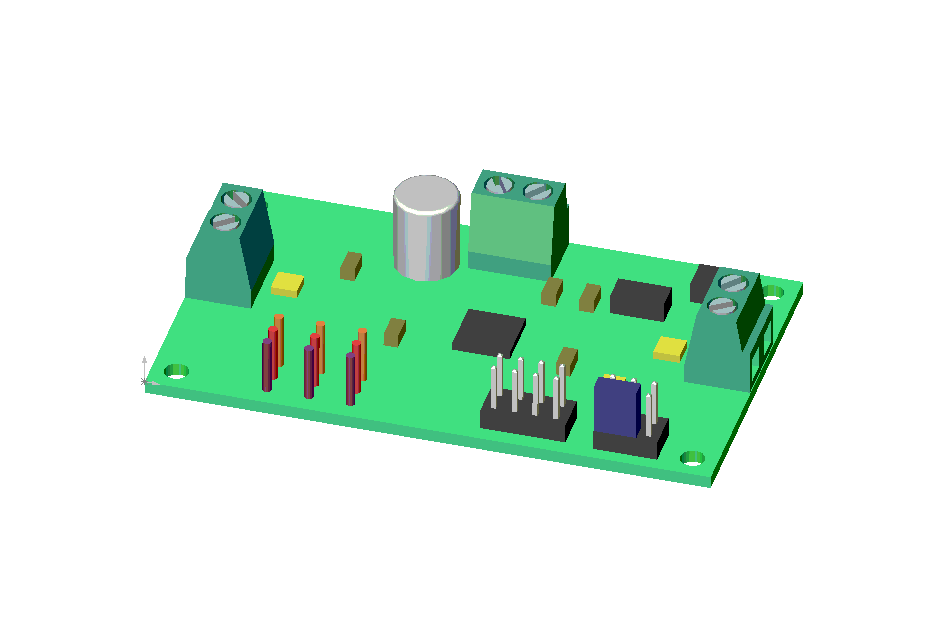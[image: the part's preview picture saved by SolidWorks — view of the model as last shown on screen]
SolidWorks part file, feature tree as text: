
SOLIDWORKS PART (.sldprt)
format: sldprt  version: not decoded by parser v0  size: 1,186,816 bytes
history: native  units: mm
features: sketch x24, extrude x15, cut_extrude x9, fillet x1, chamfer x1 (+8 scaffold rows collapsed)
feature tree (58):
  scaffold x8  (default folders/planes/origin — collapsed)
  sketch  "Sketch1"  dims[c1.D3=3.048mm c1.D4=3.05mm c1.D5=3.05mm c1.D6=3.05mm c2.D3=3.05mm c2.D1=69.0mm c2.D2=40.15mm c2.D7=3.05mm c2.D8=3.05mm c2.D9=3.05mm c2.D10=3.05mm]
  extrude  "Base-Extrude"  Depth=1.5748mm
  sketch  "Sketch2"  dims[c1.D1=12.7mm c1.D2=10.1mm c1.D3=10.1mm c1.D4=10.1mm c1.D5=8.1mm c1.D6=8.1mm c1.D7=8.1mm c1.D8=12.7mm c1.D9=28.5mm c2.D5=0.1mm c2.D6=0.1mm c2.D10=0.1mm c2.D11=8.0mm c2.D7=8.0mm c2.D12=8.0mm]
  extrude  "Boss-Extrude1"  Depth=9.94mm
  sketch  "Sketch3"  dims[c1.D1=4.3mm c1.D2=0.96mm c1.D3=1.7mm c1.D4=7.5mm c1.D5=1.45mm c1.D6=1.45mm c1.D7=7.5mm c1.D8=0.96mm c1.D9=0.96mm c2.D9=90.0deg c3.D9=1.7mm c3.D10=4.3mm]
  cut_extrude  "Cut-Extrude1"  [1 undecoded]
  sketch  "Sketch4"  dims[D1=0.96mm D2=4.3mm D3=1.7mm D4=1.45mm D5=7.5mm]
  cut_extrude  "Cut-Extrude2"  [1 undecoded]
  sketch  "Sketch5"  dims[D2=3.7mm D4=3.7mm D11=3.7mm D12=3.7mm D17=3.7mm D18=3.7mm D1=2.7mm D3=2.42mm D5=2.7mm D6=2.42mm D7=2.42mm D8=2.42mm D9=2.7mm D10=2.7mm D13=2.7mm D14=2.7mm D15=2.42mm D16=2.42mm]
  cut_extrude  "Cut-Extrude3"  Depth=2mm
  sketch  "Sketch6"  dims[D1=3.1mm D2=3.1mm D3=3.1mm D4=3.1mm D5=3.1mm D6=3.1mm]
  extrude  "Boss-Extrude4"  [1 undecoded]
  sketch  "Sketch7"  dims[c1.D7=~3.256358mm c1.D8=~3.313702mm c1.D1=0.5mm c1.D2=0.5mm c1.D3=0.5mm c1.D4=0.5mm c1.D5=10.1mm c2.D5=40.0deg c2.D6=~2.93428mm c3.D6=55.0deg c3.D2=0.5mm c4.D6=~4.719132mm c5.D6=55.0deg]
  cut_extrude  "Cut-Extrude4"  Depth=1.2mm
  sketch  "Sketch8"  dims[c1.D1=~3.324113mm c1.D2=~3.344496mm c1.D3=0.5mm c1.D4=1.0mm c1.D5=~4.793274mm c2.D5=128.0deg c2.D6=0.5mm c2.D7=1.0mm c2.D8=~4.589517mm c3.D8=~60.168045deg]
  cut_extrude  "Cut-Extrude5"  Depth=1.2mm
  sketch  "Sketch10"  dims[c1.D1=~3.328408mm c1.D2=~3.418532mm c1.D3=0.5mm c1.D4=1.0mm c1.D5=0.5mm c1.D6=1.0mm c1.D7=~4.415311mm c2.D7=50.0deg c2.D8=~4.611922mm c3.D8=48.0deg]
  cut_extrude  "Cut-Extrude6"  Depth=1.2mm
  sketch  "Sketch11"  dims[c1.D1=1.0mm c1.D2=1.0mm c1.D3=2.0mm c1.D4=1.5mm c1.D5=1.5mm c1.D6=1.0mm c1.D7=1.0mm c1.D8=3.0mm c2.D3=3.0mm]
  cut_extrude  "Cut-Extrude7"  Depth=2mm
  sketch  "Sketch12"  dims[D1=1.0mm D2=1.0mm D3=1.5mm D4=1.5mm D5=1.0mm D6=1.0mm D7=3.0mm D8=3.0mm]
  cut_extrude  "Cut-Extrude8"  Depth=2mm
  sketch  "Sketch13"  dims[D1=1.0mm D2=1.0mm D3=1.0mm D4=1.0mm D5=1.5mm D6=1.5mm D7=3.0mm D8=3.0mm]
  cut_extrude  "Cut-Extrude9"  Depth=2mm
  sketch  "Sketch14"  dims[D3=8.0mm D1=8.23mm D2=25.4mm]
  extrude  "Boss-Extrude5"  Depth=10mm
  fillet  "Fillet1"  Radius=0.5mm
  sketch  "Sketch15"  dims[D1=7.82mm D2=7.0mm D3=5.0mm D4=1.65mm D5=2.0mm D6=28.7mm D7=5.0mm D8=10.42mm]
  extrude  "Boss-Extrude6"  Depth=2.46mm
  sketch  "Sketch16"  dims[D1=0.61mm D2=0.61mm D3=0.61mm D4=0.61mm D5=2.54mm D6=2.54mm D7=2.54mm D8=0.61mm D9=1.065mm D10=0.925mm D11=0.61mm D12=0.61mm D13=0.61mm D14=0.61mm D15=0.61mm D16=0.61mm D17=2.54mm D18=2.54mm D19=2.54mm D20=0.93mm D21=1.07mm D22=2.54mm]
  extrude  "Boss-Extrude7"  Depth=6mm
  chamfer  "Chamfer2"  Distance=0.25mm Angle=45deg
  sketch  "Sketch17"  dims[D1=8.83mm D2=10.93mm D3=9.54mm D4=9.54mm D5=8.7mm D6=8.7mm D7=6.62mm D8=7.66mm D9=8.7mm]
  extrude  "Boss-Extrude8"  Depth=4.35mm
  sketch  "Sketch19"  dims[c1.D1=8.07mm c1.D2=3.66mm c1.D3=4.2mm c1.D4=3.2mm c1.D5=13.06mm c1.D6=6.53mm c1.D7=8.6mm c1.D8=3.5mm c2.D5=13.6mm c2.D7=8.6mm c2.D4=3.2mm c2.D1=8.07mm]
  extrude  "Boss-Extrude9"  Depth=2.58mm
  sketch  "Sketch20"  dims[D1=16.02mm D2=7.0mm D3=7.0mm D4=33.0mm]
  extrude  "Boss-Extrude10"  Depth=1mm
  sketch  "Sketch21"  dims[D1=1.15mm D2=1.15mm D3=1.15mm D4=5.08mm D5=5.08mm D6=2.54mm D7=14.22mm]
  extrude  "Boss-Extrude11"  Depth=7mm
  sketch  "Sketch22"  dims[D1=1.15mm D2=1.15mm D3=1.15mm D4=2.54mm]
  extrude  "Boss-Extrude12"  Depth=7mm
  sketch  "Sketch23"  dims[D1=1.15mm D2=1.15mm D3=1.15mm D4=2.54mm]
  extrude  "Boss-Extrude13"  Depth=7mm
  sketch  "Sketch24"  dims[D1=12.73mm D2=12.73mm D3=16.17mm D4=16.17mm D5=3.2mm D6=3.2mm D7=3.2mm D8=3.2mm D9=15.0mm D10=14.5mm D11=1.6mm D12=2.64mm]
  extrude  "Boss-Extrude14"  Depth=1mm
  sketch  "Sketch25"  dims[D1=22.0mm D2=1.75mm D3=1.75mm D4=3.35mm D5=3.35mm D6=9.29mm D7=9.29mm D8=28.4mm D9=23.0mm D10=1.75mm D11=3.35mm D12=22.15mm D13=3.35mm D14=3.35mm D15=1.75mm D16=1.75mm D17=25.0mm D18=16.57mm D19=10.9mm]
  extrude  "Boss-Extrude15"  Depth=1.63mm
  sketch  "Sketch26"  dims[c1.D1=1.0mm c1.D2=~2.103898mm c1.D3=2.01mm c1.D4=1.0mm c1.D5=0.7mm c2.D2=0.7mm]
  extrude  "Boss-Extrude16"  Depth=6.5mm
decode coverage: 47 of 50 modeling features carry decoded parameters
note: ~ marks probable driven/reference dimensions
note: 3 parameter values undecoded
summary: no parameter record found for 3 features
note: suppression state not decoded; provenance and decode notes live in map.json
